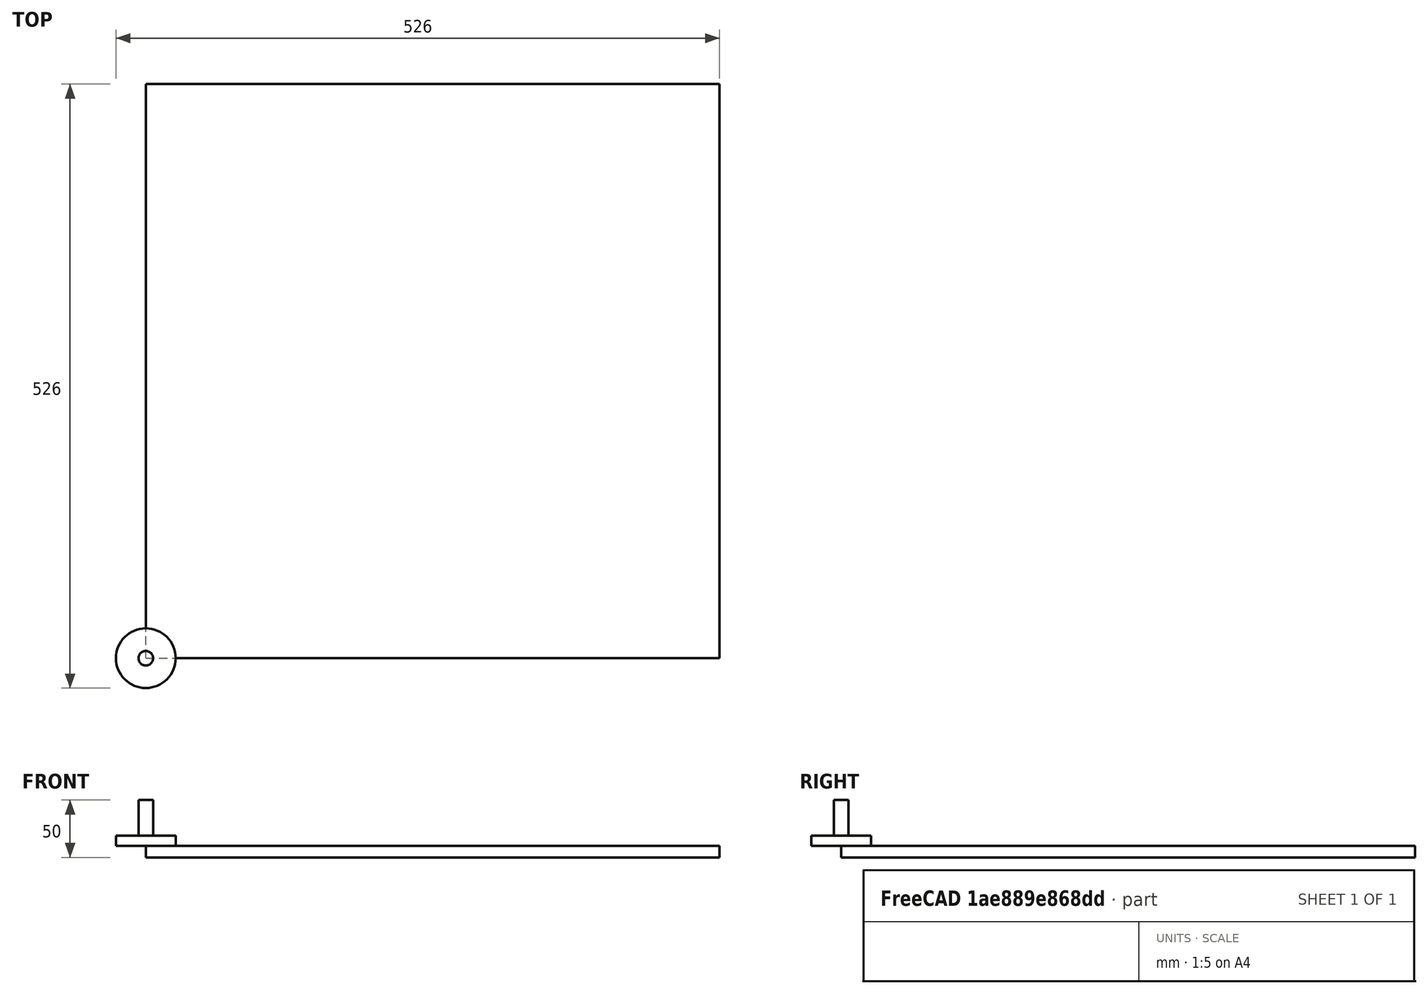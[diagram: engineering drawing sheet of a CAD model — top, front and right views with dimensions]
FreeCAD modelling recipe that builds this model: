
FCSTD DOCUMENT  (FreeCAD 0.19R14555 (Git shallow))
Label: HalfMetreSquare
License: All rights reserved
LicenseURL: http://en.wikipedia.org/wiki/All_rights_reserved
objects: Part::FeaturePython×3, Path::FeaturePython×3, App::DocumentObjectGroup×2, Sketcher::SketchObject×1, PartDesign::Pad×1, PartDesign::Body×1, App::FeaturePython×1, Path::FeatureCompoundPython×1, Mesh::FeaturePython×1
note: 8 computed .brp shape members not serialized (recipe doc carries the construction recipe); baked Part::Feature solids carry a one-line shape summary decoded from their .brp

FEATURE [Sketcher::SketchObject] Sketch
  FullyConstrained = true
  MapMode = 5
  Support = -> [XY_Plane]
  sketch-geometry (4):
    g0: LineSegment StartX=0 StartY=500 StartZ=0 EndX=500 EndY=500 EndZ=0
    g1: LineSegment StartX=500 StartY=500 StartZ=0 EndX=500 EndY=0 EndZ=0
    g2: LineSegment StartX=500 StartY=0 StartZ=0 EndX=0 EndY=0 EndZ=0
    g3: LineSegment StartX=0 StartY=0 StartZ=0 EndX=0 EndY=500 EndZ=0
  constraints (11):
    c: Coincident(g0,g1)
    c: Coincident(g1,g2)
    c: Coincident(g2,g3)
    c: Coincident(g3,g0)
    c: Horizontal(g0)
    c: Horizontal(g2)
    c: Vertical(g1)
    c: Vertical(g3)
    c: Coincident(g-1,g2)
    c: DistanceX(g2,g2) = 500
    c: DistanceY(g3,g3) = 500
FEATURE [PartDesign::Pad] Pad
  Direction = (1,1,1)
  Length = 10
  Length2 = 100
  Profile = -> Sketch
  Reversed = true
  Type = 0
FEATURE [PartDesign::Body] Body
  Group = -> [Sketch,Pad]
  Origin = -> Origin
  Tip = -> Pad
FEATURE [App::FeaturePython] SetupSheet  # Path/CAM operation (typed FeaturePython)
  ClearanceHeightExpression = OpStockZMax+SetupSheet.ClearanceHeightOffset
  ClearanceHeightOffset = 5
  CoolantMode = 0
  CoolantModes = None | Flood | Mist
  FinalDepthExpression = OpFinalDepth
  HorizRapid = 0
  SafeHeightExpression = OpStockZMax+SetupSheet.SafeHeightOffset
  SafeHeightOffset = 3
  StartDepthExpression = OpStartDepth
  StepDownExpression = OpToolDiameter
  VertRapid = 0
FEATURE [Part::FeaturePython] Clone  label="Model-Body"  # Draft clone (typed FeaturePython)
  AttacherType = Attacher::AttachEngine3D
  Fuse = false
  Objects = -> [Body]
  PathResource = Model
  Scale = (1,1,1)
FEATURE [App::DocumentObjectGroup] Model
  Group = -> [Clone]
FEATURE [Part::FeaturePython] Stock001  # WARN: FeaturePython — macro-defined, semantics opaque (R4)
  Height = 10
  Length = 500
  Placement = pos=(0,0,-10) rot=(0,0,1;0rad)
  StockType = CreateBox
  Width = 500
FEATURE [Part::FeaturePython] ToolBit001  label="52mm Endmill"  # Path/CAM toolbit (typed FeaturePython)
  BitPropertyNames = Chipload | CuttingEdgeHeight | Diameter | Flutes | Length | Material | ShankDiameter
  BitShape = /app/freecad/Mod/Path/Tools/Shape/endmill.fcstd
  Chipload = 0
  CuttingEdgeHeight = 9
  Diameter = 52
  File = <userpath>/Documents/MensShed/FreeCAD/Bit/52mm_EndMill.fctb
  Flutes = 0
  Length = 40
  Material = 0
  ShankDiameter = 12.7
  ShapeName = endmill
FEATURE [Path::FeaturePython] _2mm_Endmill  label="52mm Endmill001"  # Path/CAM operation (typed FeaturePython)
  HorizFeed = 40
  HorizRapid = 0
  SpindleDir = 0
  SpindleSpeed = 10000
  Tool = -> ToolBit001
  ToolNumber = 1
  VertFeed = 40
  VertRapid = 0
  expr: HorizRapid = SetupSheet.HorizRapid
  expr: VertRapid = SetupSheet.VertRapid
FEATURE [App::DocumentObjectGroup] Tools
  Group = -> [_2mm_Endmill]
FEATURE [Path::FeaturePython] MillFace  # Path/CAM operation (typed FeaturePython)
  Active = true
  AreaParams:
    Tolerance = 1e-07
    FitArcs = True
    Simplify = False
    CleanDistance = 0.0
    Accuracy = 0.01
    Unit = 1.0
    MinArcPoints = 4
    MaxArcPoints = 100
    ClipperScale = 10000000.0
    Fill = 0
    Coplanar = 0
    Reorient = True
    Outline = False
    Explode = False
    OpenMode = 0
    Deflection = 0.01
    SubjectFill = 0
    ClipFill = 0
    Offset = 0.0
    ExtraPass = 0
    Stepover = 0.0
    LastStepover = 0.0
    JoinType = 0
    EndType = 0
    MiterLimit = 2.0
    RoundPrecision = 0.0
    PocketMode = 2
    ToolRadius = 26.0
    PocketExtraOffset = 0.0
    PocketStepover = 39.0
    PocketLastStepover = 0.0
    FromCenter = True
    Angle = 45.0
    AngleShift = 0.0
    Shift = 0.0
    Thicken = False
    SectionCount = -1
    Stepdown = 1.0
    SectionOffset = 0.0
    SectionTolerance = 1e-06
    SectionMode = 2
    Project = False
  Base = -> [Clone]
  BoundaryShape = 0
  ClearEdges = false
  ClearanceHeight = 5
  CoolantMode = None
  CutMode = 0
  CycleTime = 00:05:45
  EnableRotation = 0
  ExcludeRaisedAreas = false
  ExtraOffset = 0
  FinalDepth = -0.5
  FinishDepth = 0.1
  KeepToolDown = false
  MinTravel = false
  OffsetPattern = 1
  OpFinalDepth = 0
  OpStartDepth = 0.5
  OpStockZMax = 0
  OpStockZMin = -10
  OpToolDiameter = 52
  PathParams = {'orientation': 1, 'feedrate': 40.0, 'feedrate_v': 40.0, 'verbose': True, 'resume_height': 3.0, 'retraction': 5.0, 'return_end': True, 'preamble': False}
  SafeHeight = 3
  StartAt = 0
  StartDepth = 0
  StartPoint = (0,0,0)
  StepDown = 0.5
  StepOver = 75
  ToolController = -> _2mm_Endmill
  UseStartPoint = false
  ZigZagAngle = 45
  expr: FinishDepth = 0.1mm
  expr: ClearanceHeight = OpStockZMax + SetupSheet.ClearanceHeightOffset
  expr: SafeHeight = OpStockZMax + SetupSheet.SafeHeightOffset
  expr: StepDown = 0.5mm
  expr: FinalDepth = -0.5mm
  expr: StartDepth = 0
FEATURE [Path::FeatureCompoundPython] Operations  # Path/CAM operation (typed FeaturePython)
  Group = -> [MillFace]
  UsePlacements = false
FEATURE [Path::FeaturePython] Job  # Path/CAM operation (typed FeaturePython)
  CycleTime = 00:05:45
  Fixtures = G54
  GeometryTolerance = 0.01
  LastPostProcessDate = 2021-12-14 08:41:43.963939
  LastPostProcessOutput = <userpath>/Documents/MensShed/HalfMetreSquare.ngc
  Model = -> Model
  Operations = -> Operations
  OrderOutputBy = 0
  PostProcessor = 7
  PostProcessorOutputFile = <userpath>/Documents/MensShed/HalfMetreSquare.ngc
  SetupSheet = -> SetupSheet
  SplitOutput = false
  Stock = -> Stock001
  Tools = -> Tools
FEATURE [Mesh::FeaturePython] CutMaterial  # WARN: FeaturePython — macro-defined, semantics opaque (R4)
